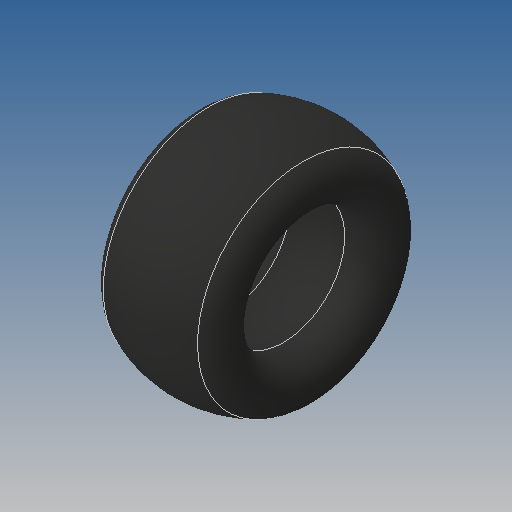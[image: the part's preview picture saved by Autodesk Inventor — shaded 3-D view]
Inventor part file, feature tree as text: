
AUTODESK INVENTOR PART (.ipt)
format: ipt  version: 2020 (Build 240168000, 168)  size: 201,216 bytes
history: native  units: mm
features: sketch x2, other x1, sweep x1
ambient origin geometry x8: Origin, YZ Plane, XZ Plane, XY Plane, X Axis, Y Axis, Z Axis, Center Point
bodies: Body1 (feature_tree)
feature tree (4):
  other  "Твердое тело1"
  sweep  "Сдвиг1"
  sketch  "Эскиз1"
  sketch  "Эскиз2"
